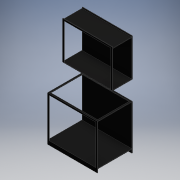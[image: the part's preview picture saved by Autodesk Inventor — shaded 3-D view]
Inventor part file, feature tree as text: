
AUTODESK INVENTOR PART (.ipt)
format: ipt  version: 2016 (Build 200138000, 138)  size: 257,536 bytes
history: native  units: mm
features: extrude x9, projected_geometry x9, sketch x8, plane x1
ambient origin geometry x8: Origin, YZ Plane, XZ Plane, XY Plane, X Axis, Y Axis, Z Axis, Center Point
bodies: Solid1 (feature_tree)
feature tree (27):
  extrude  "Extrusion1"  Depth=10.0mm
  extrude  "Extrusion2"  Depth=80.0mm
  extrude  "Extrusion3"  Depth=30.0mm
  extrude  "Extrusion4"  Depth=30.0mm
  plane  "Work Plane1"
  extrude  "Extrusion5"  Depth=10.0mm
  extrude  "Extrusion9"  Depth=10.0mm
  extrude  "Extrusión10"  Depth=30.0mm
  extrude  "Extrusión11"  TaperAngle=0.0deg  [1 undecoded]
  extrude  "Extrusion13"  Depth=1483.333333mm
  sketch  "Sketch1"  dims[d3=0.0mm d5=10.0mm]
  sketch  "Sketch2"  dims[d6=10.0mm d7=80.0mm]
  projected_geometry  "Projected Loop1"
  sketch  "Sketch3"  dims[d9=0.0mm d10=30.0mm]
  projected_geometry  "Projected Loop2"
  sketch  "Sketch4"  dims[d11=400.0mm d12=0.0mm d13=30.0mm]
  projected_geometry  "Projected Loop3"
  projected_geometry  "Projected Loop4"
  projected_geometry  "Projected Loop5"
  sketch  "Sketch5"  dims[d14=30.0mm d15=10.0mm]
  sketch  "Sketch9"  dims[d16=0.0mm d18=10.0mm]
  projected_geometry  "Projected Loop9"
  sketch  "Boceto10"  dims[d19=0.0mm d32=30.0mm]
  projected_geometry  "Contorno proyectado10"
  projected_geometry  "Contorno proyectado11"
  sketch  "Sketch13"  dims[d33=10.0mm d34=0.0mm d36=1483.333333mm d39=10.0mm d40=10.0mm d41=10.0mm d43=0.0mm d44=30.0mm d45=30.0mm d46=30.0mm d48=750.0mm d49=0.0mm d53=10.0mm d54=20.0mm d55=1483.333333mm d56=0.0mm]
  projected_geometry  "Projected Loop12"
note: 1 required parameter value undecoded (feature->parameter linkage not recoverable at this tier; creation-order binding heuristic only, values carry confidence <= 0.55)
